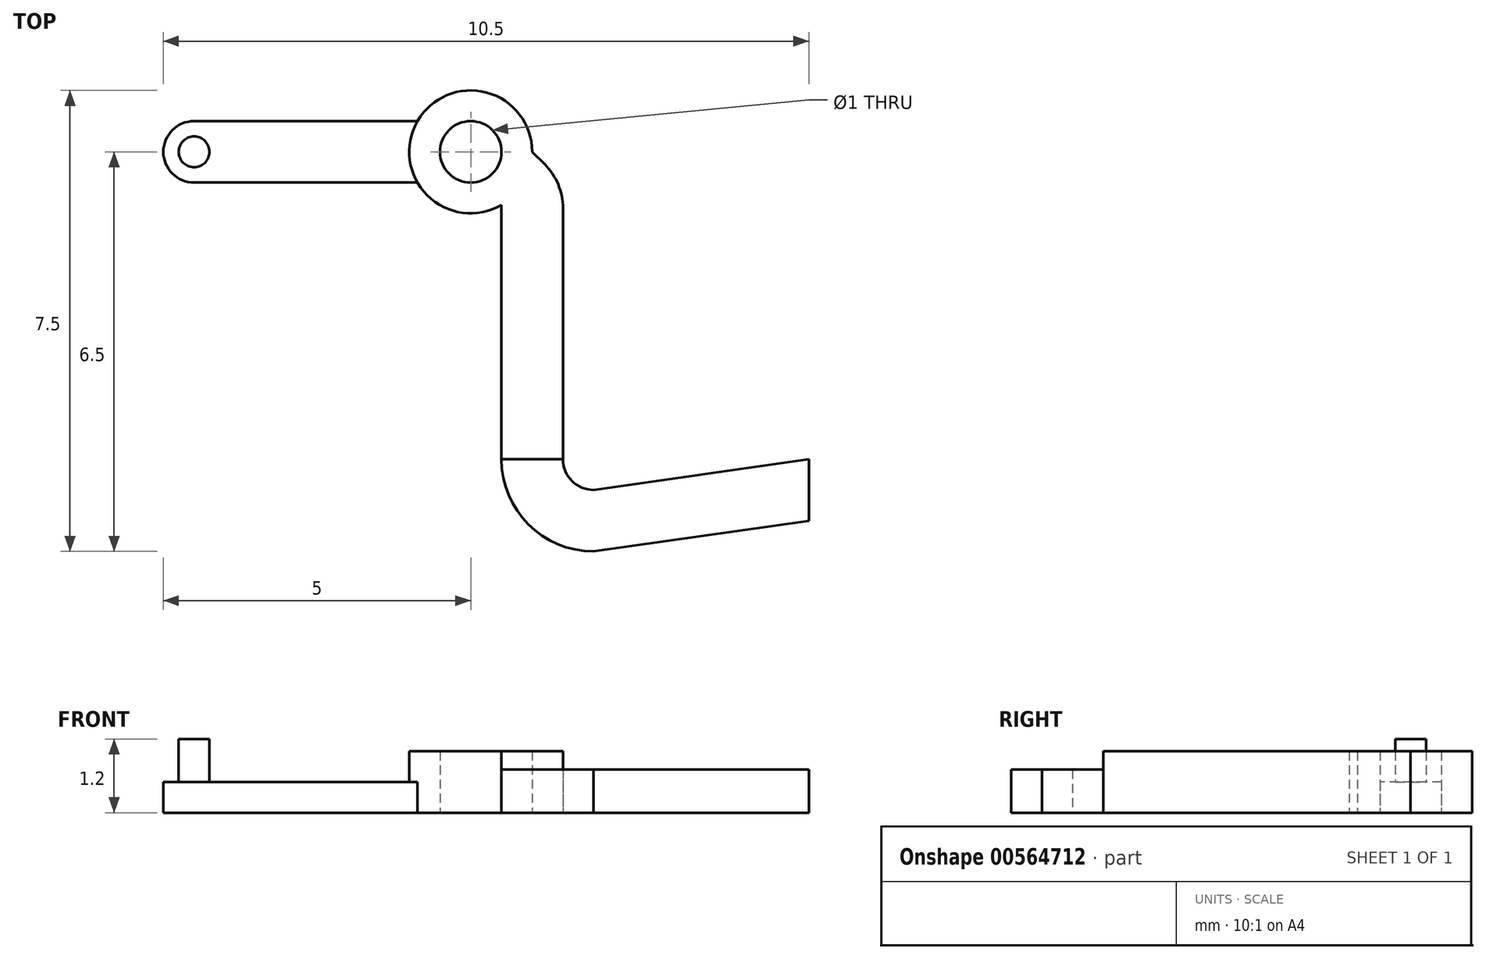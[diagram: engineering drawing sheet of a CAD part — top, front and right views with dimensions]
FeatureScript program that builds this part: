
annotation { "Feature Type Name" : "Feature", "Feature Type Description" : "" }
export const myFeature = defineFeature(function(context is Context, id is Id, definition is map)
    precondition{}
    {
        {
            var Q0;
            Q0=qCreatedBy(makeId("Top.planeOp"),FACE);
            var sketch = newSketch(context, id + "F0", { "sketchPlane" : qUnion([Q0])});
            skLineSegment(sketch, "E0", {"start": v(-0.5, 4.13) * mm, "end": v(-0.5, 0) * mm});
            skLineSegment(sketch, "E1.MirrorCS", {"start": v(0.5, 4.09) * mm, "end": v(0.5, 0) * mm});
            skCircle(sketch, "E2", {"center": v(-1, 5) * mm, "radius": 0.5 * mm});
            skArc(sketch, "E3", {"start": v(0, 5) * mm, "mid": v(-1.87, 5.5) * mm, "end": v(-0.5, 4.13) * mm});
            skLineSegment(sketch, "E4", {"start": v(0.2, 4.8) * mm, "end": v(0, 5) * mm});
            skPoint(sketch, "E5.visualSharp", {"position": v(0.5, 4.5) * mm});
            skArc(sketch, "E5.filletArc", {"start": v(0.5, 4.09) * mm, "mid": v(0.42, 4.47) * mm, "end": v(0.2, 4.8) * mm});
            skPoint(sketch, "E6.orphan", {"position": v(-0.5, 4.5) * mm});
            skArc(sketch, "E7", {"start": v(0.5, 0) * mm, "mid": v(0.65, -0.35) * mm, "end": v(1, -0.5) * mm});
            skArc(sketch, "E8", {"start": v(-0.5, 0) * mm, "mid": v(-0.06, -1.06) * mm, "end": v(1, -1.5) * mm});
            skLineSegment(sketch, "E9", {"start": v(1, -0.5) * mm, "end": v(4.5, 0) * mm});
            skLineSegment(sketch, "E10", {"start": v(1, -1.5) * mm, "end": v(4.5, -1) * mm});
            skLineSegment(sketch, "E11", {"start": v(4.5, -1) * mm, "end": v(4.5, 0) * mm});
            skLineSegment(sketch, "E12", {"start": v(-5.5, 5.5) * mm, "end": v(-1.87, 5.5) * mm});
            skLineSegment(sketch, "E13", {"start": v(-5.5, 4.5) * mm, "end": v(-1.87, 4.5) * mm});
            skArc(sketch, "E14", {"start": v(-5.5, 5.5) * mm, "mid": v(-6, 5) * mm, "end": v(-5.5, 4.5) * mm});
            skCircle(sketch, "E15", {"center": v(-5.5, 5) * mm, "radius": 0.25 * mm});
            skLineSegment(sketch, "E16", {"start": v(-0.5, 0) * mm, "end": v(0.5, 0) * mm});
            skLineSegment(sketch, "E17", {"start": v(4, -0.07) * mm, "end": v(4, -1.07) * mm});
            skSolve(sketch);
        }
        {
            var Q0;
            {var subQ1=sQuery(id+"F0.wireOp",EDGE,"E12");Q0=makeQuery(id+"F0.imprint","IMPRINT",FACE,{"disambiguationData":[TD([[makeQuery(id+"F0.imprint","IMPRINT",EDGE,{"derivedFrom":subQ1}),-1.0]])]});}
            extrude(context, id + "F1", {"entities" : qUnion([Q0]), "depth" : 0.5 * mm, "offsetDistance" : 25 * mm});
        }
        {
            var Q0;
            {var subQ3=sQuery(id+"F0.wireOp",EDGE,"E0");Q0=makeQuery(id+"F0.imprint","IMPRINT",FACE,{"disambiguationData":[TD([[makeQuery(id+"F0.imprint","IMPRINT",EDGE,{"derivedFrom":subQ3}),1.0]])]});}
            extrude(context, id + "F2", {"entities" : qUnion([Q0]), "operationType" : NewBodyOperationType.ADD, "depth" : 1 * mm, "offsetDistance" : 25 * mm});
        }
        {
            var Q0;
            {var subQ4=sQuery(id+"F0.wireOp",EDGE,"E7");Q0=makeQuery(id+"F0.imprint","IMPRINT",FACE,{"disambiguationData":[TD([[makeQuery(id+"F0.imprint","IMPRINT",EDGE,{"derivedFrom":subQ4}),-1.0]])]});}
            extrude(context, id + "F3", {"entities" : qUnion([Q0]), "operationType" : NewBodyOperationType.ADD, "depth" : 0.7 * mm, "offsetDistance" : 25 * mm});
        }
        {
            var Q0;
            {var subQ0=sQuery(id+"F0.wireOp",EDGE,"E11");Q0=makeQuery(id+"F0.imprint","IMPRINT",FACE,{"disambiguationData":[TD([[makeQuery(id+"F0.imprint","IMPRINT",EDGE,{"derivedFrom":subQ0}),1.0]])]});}
            var Q1;
            Q1=makeQuery(id+"F3.opExtrude","CAP_FACE",FACE,{"disambiguationData":[OSD([sQuery(id+"F0.wireOp",EDGE,"E7"),sQuery(id+"F0.wireOp",EDGE,"E8"),sQuery(id+"F0.wireOp",EDGE,"E9"),sQuery(id+"F0.wireOp",EDGE,"E10"),sQuery(id+"F0.wireOp",EDGE,"E16"),sQuery(id+"F0.wireOp",EDGE,"E17")])],"isStart":false});
            extrude(context, id + "F4", {"entities" : qUnion([Q0]), "operationType" : NewBodyOperationType.ADD, "endBound" : BoundingType.UP_TO_SURFACE, "depth" : 25 * mm, "endBoundEntityFace" : qUnion([Q1]), "offsetDistance" : 25 * mm});
        }
        {
            var Q0;
            Q0=makeQuery(id+"F0.imprint","IMPRINT",FACE,{"disambiguationData":[TD([[makeQuery(id+"F0.imprint","IMPRINT",EDGE,{"derivedFrom":sQuery(id+"F0.wireOp",EDGE,"E15")}),1.0]])]});
            extrude(context, id + "F5", {"entities" : qUnion([Q0]), "operationType" : NewBodyOperationType.ADD, "depth" : 1.2 * mm, "offsetDistance" : 25 * mm});
        }
    });
